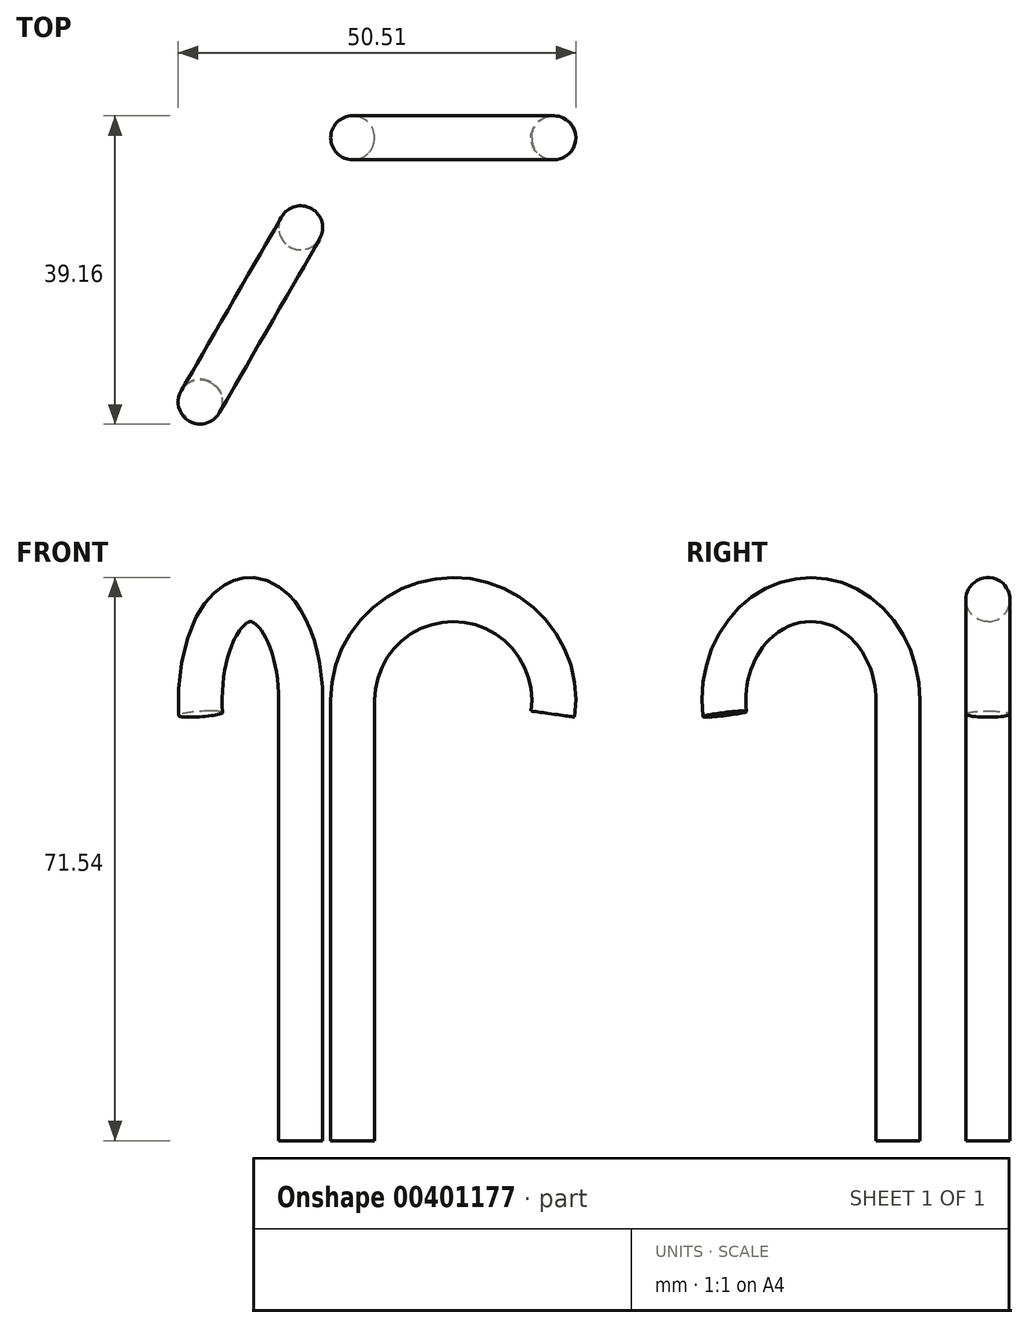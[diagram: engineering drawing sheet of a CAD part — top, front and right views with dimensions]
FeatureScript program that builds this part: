
annotation { "Feature Type Name" : "Feature", "Feature Type Description" : "" }
export const myFeature = defineFeature(function(context is Context, id is Id, definition is map)
    precondition{}
    {
        {
            var Q0;
            Q0=qCreatedBy(makeId("Front.planeOp"),FACE);
            var sketch = newSketch(context, id + "F0", { "sketchPlane" : qUnion([Q0])});
            skLineSegment(sketch, "E0", {"start": v(0, 0) * mm, "end": v(0, 55.97) * mm});
            skArc(sketch, "E1", {"start": v(0, 55.97) * mm, "mid": v(13.66, 68.7) * mm, "end": v(25.42, 54.2) * mm});
            skSolve(sketch);
        }
        {
            var Q0;
            Q0=qCreatedBy(makeId("Top.planeOp"),FACE);
            var sketch = newSketch(context, id + "F1", { "sketchPlane" : qUnion([Q0])});
            skCircle(sketch, "E2", {"center": v(0, 0) * mm, "radius": 2.8 * mm});
            skSolve(sketch);
        }
        {
            var Q0;
            Q0=makeQuery(id+"F1.imprint","IMPRINT",FACE,{"disambiguationData":[TD([[makeQuery(id+"F1.imprint","IMPRINT",EDGE,{"derivedFrom":sQuery(id+"F1.wireOp",EDGE,"E2")}),1.0]])]});
            var Q1;
            Q1=sQuery(id+"F0.wireOp",EDGE,"E0");
            var Q2;
            Q2=sQuery(id+"F0.wireOp",EDGE,"E1");
            sweep(context, id + "F2", {"profiles" : qUnion([Q0]), "path" : qUnion([Q1, Q2])});
        }
        {
            var Q0;
            Q0=makeQuery(id+"F2.opSweep","SWEPT_BODY",BODY,{"disambiguationData":[OSD([sQuery(id+"F0.wireOp",EDGE,"E1"),sQuery(id+"F1.wireOp",EDGE,"E2")])]});
            var Q1;
            Q1=qCreatedBy(makeId("Right.planeOp"),FACE);
            mirror(context, id + "F3", {"entities" : qUnion([Q0]), "mirrorPlane" : qUnion([Q1])});
        }
        {
            var Q0;
            Q0=makeQuery(id+"F3.opPattern","COPY",BODY,{"derivedFrom":makeQuery(id+"F2.opSweep","SWEPT_BODY",BODY,{"disambiguationData":[OSD([sQuery(id+"F0.wireOp",EDGE,"E1"),sQuery(id+"F1.wireOp",EDGE,"E2")])]}),"instanceName":"1"});
            transform(context, id + "F4", {"entities" : qUnion([Q0]), "transformType" : TransformType.TRANSLATION_3D, "dx" : -13.2 * mm, "dy" : 0 * mm, "dz" : 0 * mm, "makeCopy" : false});
        }
        {
            var Q0;
            Q0=makeQuery(id+"F3.opPattern","COPY",BODY,{"derivedFrom":makeQuery(id+"F2.opSweep","SWEPT_BODY",BODY,{"disambiguationData":[OSD([sQuery(id+"F0.wireOp",EDGE,"E1"),sQuery(id+"F1.wireOp",EDGE,"E2")])]}),"instanceName":"1"});
            var Q1;
            Q1=makeQuery(id+"F2.opSweep","CAP_EDGE",EDGE,{"disambiguationData":[OSD([sQuery(id+"F0.wireOp",VERTEX,"E0.start"),sQuery(id+"F1.wireOp",EDGE,"E2")])],"isStart":true});
            transform(context, id + "F5", {"entities" : qUnion([Q0]), "transformType" : TransformType.ROTATION, "transformAxis" : qUnion([Q1]), "angle" : 60 * degree, "makeCopy" : false});
        }
    });
